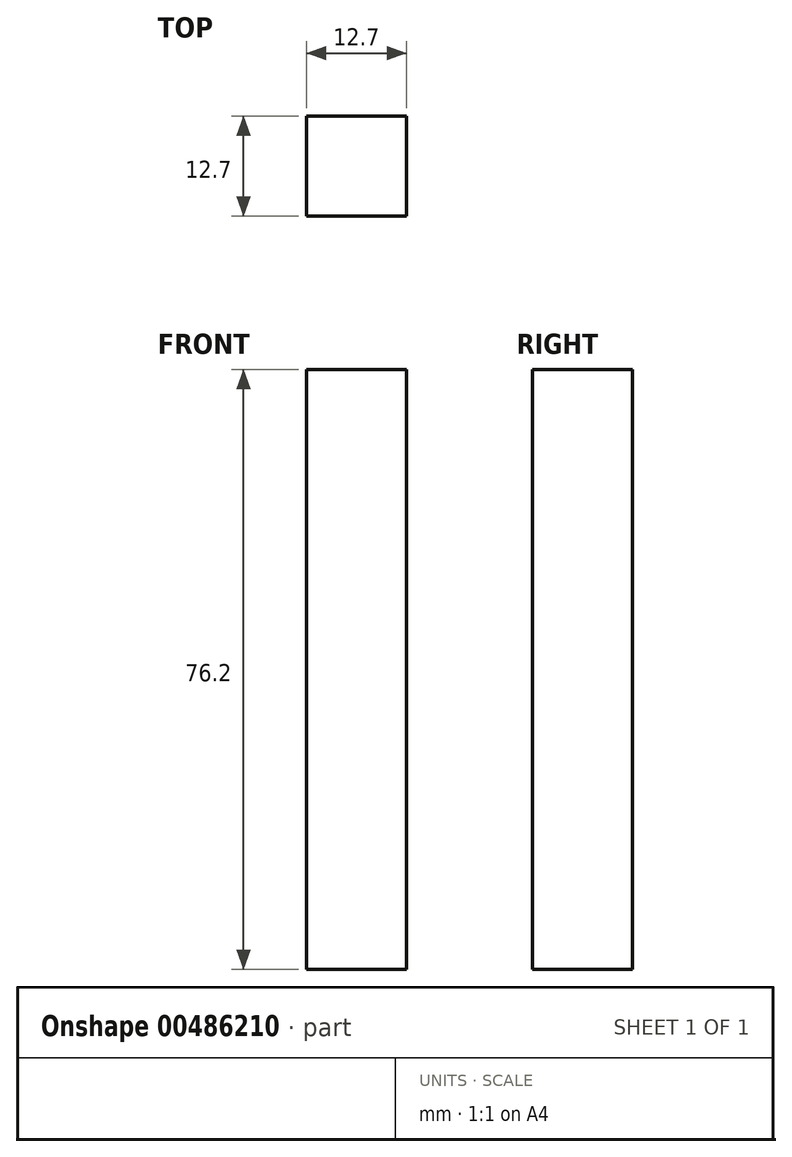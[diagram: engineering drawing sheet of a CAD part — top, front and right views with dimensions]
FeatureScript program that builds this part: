
annotation { "Feature Type Name" : "Feature", "Feature Type Description" : "" }
export const myFeature = defineFeature(function(context is Context, id is Id, definition is map)
    precondition{}
    {
        {
            var Q0;
            Q0=qCreatedBy(makeId("Top.planeOp"),FACE);
            var sketch = newSketch(context, id + "F0", { "sketchPlane" : qUnion([Q0])});
            skLineSegment(sketch, "E0.bottom", {"start": v(-44.9, 19.28) * mm, "end": v(-32.2, 19.28) * mm});
            skLineSegment(sketch, "E0.top", {"start": v(-44.9, 31.98) * mm, "end": v(-32.2, 31.98) * mm});
            skLineSegment(sketch, "E0.left", {"start": v(-44.9, 19.28) * mm, "end": v(-44.9, 31.98) * mm});
            skLineSegment(sketch, "E0.right", {"start": v(-32.2, 19.28) * mm, "end": v(-32.2, 31.98) * mm});
            skSolve(sketch);
        }
        {
            var Q0;
            Q0 = qSketchRegion(id + "F0", true);
            extrude(context, id + "F1", {"entities" : qUnion([Q0]), "depth" : 76.2 * mm, "offsetDistance" : 25.4 * mm});
        }
    });
